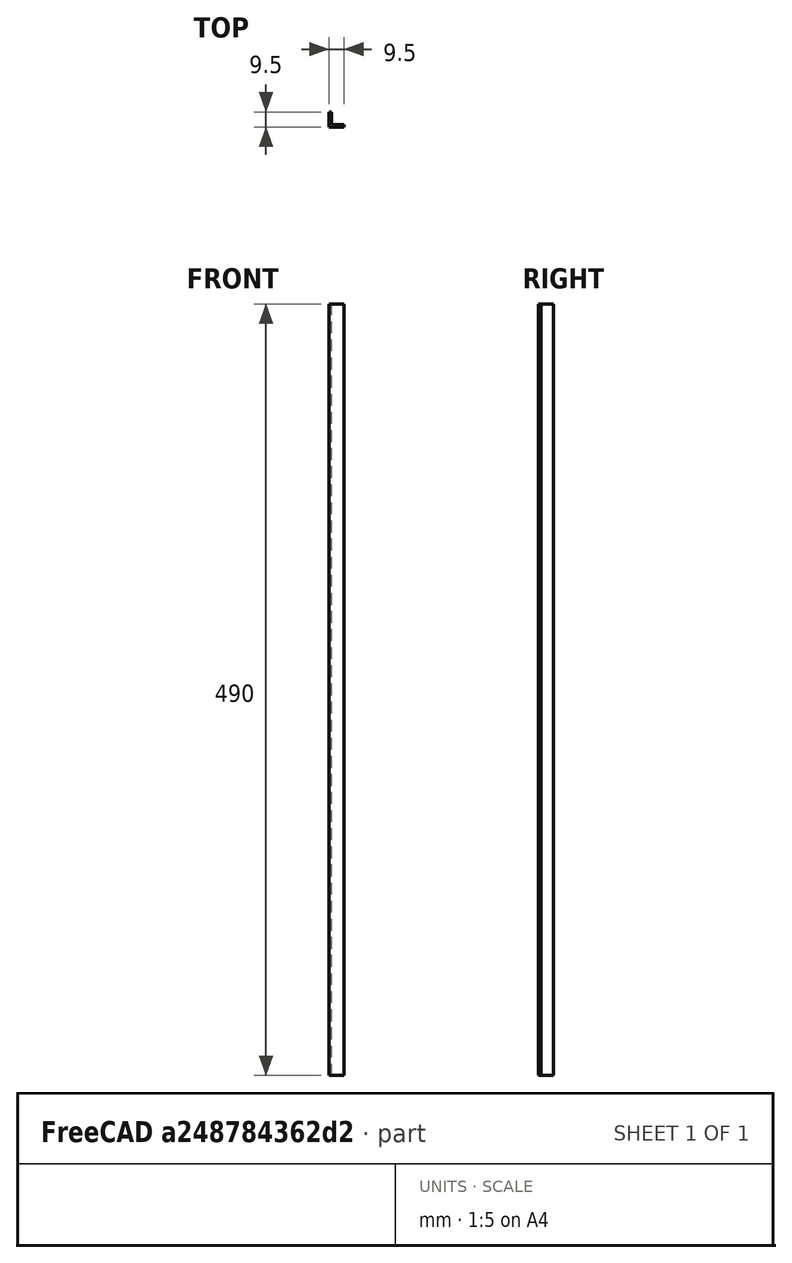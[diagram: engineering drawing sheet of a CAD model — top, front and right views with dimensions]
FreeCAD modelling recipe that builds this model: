
FCSTD DOCUMENT  (FreeCAD 0.21R33668 +7 (Git))
Label: L-front
License: All rights reserved
LicenseURL: http://en.wikipedia.org/wiki/All_rights_reserved
objects: Sketcher::SketchObject×1, PartDesign::Pad×1, PartDesign::Body×1, PartDesign::CoordinateSystem×1, App::Part×1
note: 5 computed .brp shape members not serialized (recipe doc carries the construction recipe); baked Part::Feature solids carry a one-line shape summary decoded from their .brp
EXTERNAL_REF file=planB.FCStd obj=Spreadsheet

FEATURE [Sketcher::SketchObject] Sketch
  FullyConstrained = true
  MapMode = 5
  Support = -> [XY_Plane]
  expr: Constraints[14] = planB#<<data>>.L_thickness
  expr: Constraints[16] = planB#<<data>>.L_size
  sketch-geometry (6):
    g0: LineSegment StartX=0 StartY=0 StartZ=0 EndX=0 EndY=9.5 EndZ=0
    g1: LineSegment StartX=0 StartY=9.5 StartZ=0 EndX=1.6 EndY=9.5 EndZ=0
    g2: LineSegment StartX=1.6 StartY=9.5 StartZ=0 EndX=1.6 EndY=1.6 EndZ=0
    g3: LineSegment StartX=1.6 StartY=1.6 StartZ=0 EndX=9.5 EndY=1.6 EndZ=0
    g4: LineSegment StartX=9.5 StartY=1.6 StartZ=0 EndX=9.5 EndY=0 EndZ=0
    g5: LineSegment StartX=9.5 StartY=0 StartZ=0 EndX=0 EndY=0 EndZ=0
  constraints (17):
    c: Coincident(g-1,g0)
    c: PointOnObject(g0,g-2)
    c: Coincident(g0,g1)
    c: Horizontal(g1)
    c: Coincident(g1,g2)
    c: Vertical(g2)
    c: Coincident(g2,g3)
    c: Horizontal(g3)
    c: Coincident(g3,g4)
    c: PointOnObject(g4,g-1)
    c: Vertical(g4)
    c: Coincident(g4,g5)
    c: Coincident(g5,g0)
    c: Equal(g4,g1)
    c: Distance(g1) = 1.6
    c: Equal(g0,g5)
    c: Distance(g0) = 9.5
FEATURE [PartDesign::Pad] Pad
  Direction = (0,0,1)
  Length = 490
  Length2 = 10
  Profile = -> Sketch
  ReferenceAxis = -> Sketch [N_Axis]
  Type = 0
  expr: Length = planB#<<data>>.case_w - 10
FEATURE [PartDesign::Body] Body
  Group = -> [Sketch,Pad]
  Origin = -> Origin
  Tip = -> Pad
FEATURE [PartDesign::CoordinateSystem] LCS_0
  AttacherType = Attacher::AttachEngine3D
  MapMode = 2
  Support = -> [X_Axis001]
FEATURE [App::Part] L_front
  Group = -> [LCS_0,Body]
  Origin = -> Origin001
